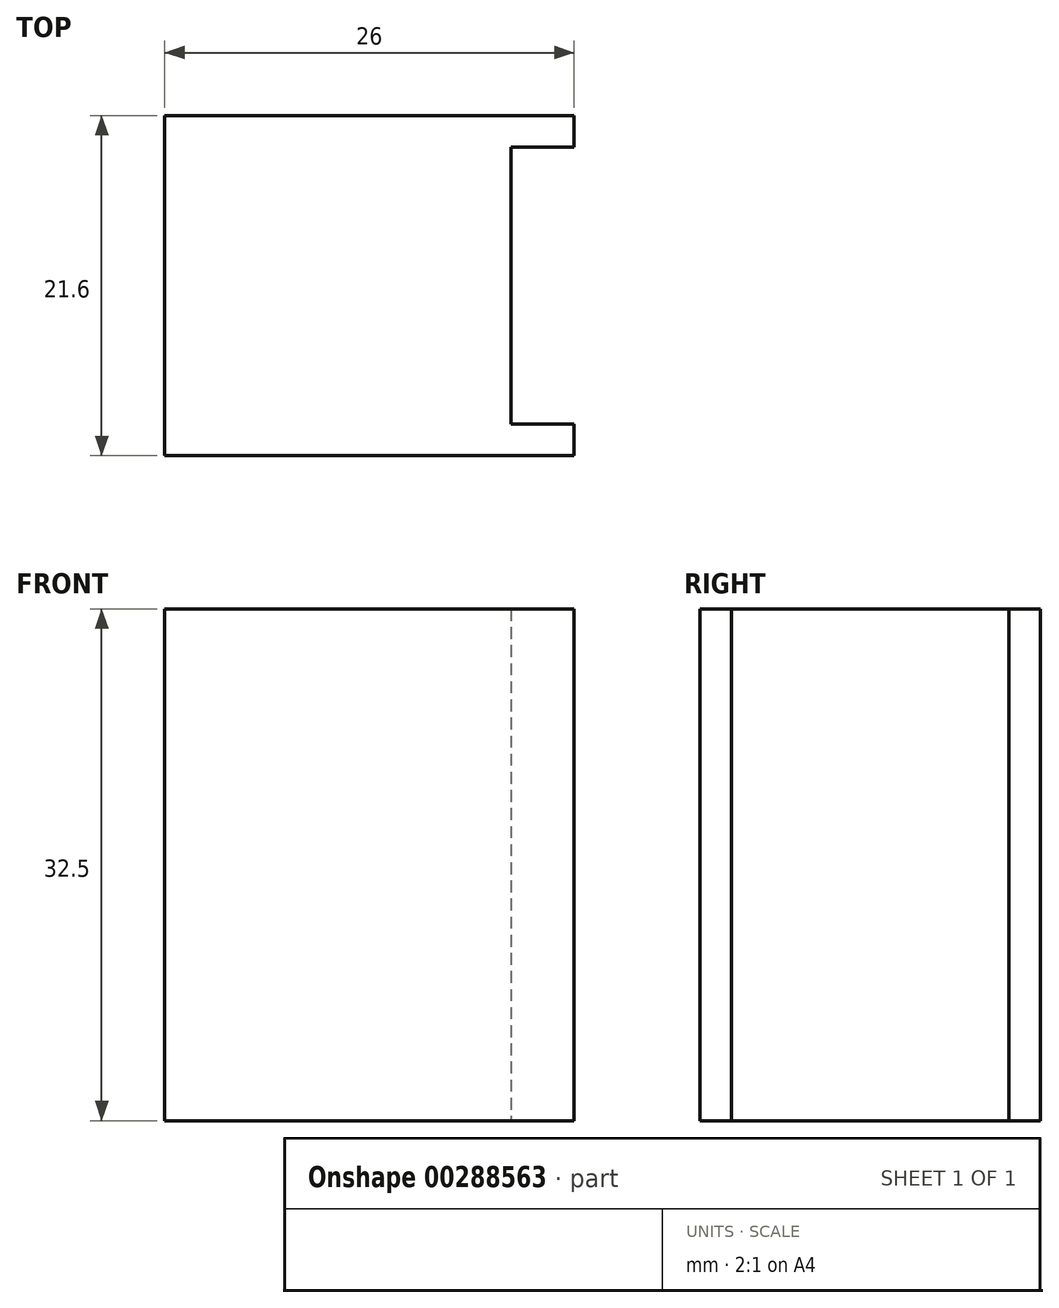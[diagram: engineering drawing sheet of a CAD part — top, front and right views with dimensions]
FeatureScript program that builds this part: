
annotation { "Feature Type Name" : "Feature", "Feature Type Description" : "" }
export const myFeature = defineFeature(function(context is Context, id is Id, definition is map)
    precondition{}
    {
        {
            var Q0;
            Q0=qCreatedBy(makeId("Top.planeOp"),FACE);
            var sketch = newSketch(context, id + "F0", { "sketchPlane" : qUnion([Q0])});
            skLineSegment(sketch, "E0.bottom", {"start": v(11, 10.8) * mm, "end": v(-11, 10.8) * mm});
            skLineSegment(sketch, "E0.top", {"start": v(11, -10.8) * mm, "end": v(-11, -10.8) * mm});
            skLineSegment(sketch, "E0.left", {"start": v(11, 10.8) * mm, "end": v(11, -10.8) * mm});
            skLineSegment(sketch, "E0.right", {"start": v(-11, 10.8) * mm, "end": v(-11, -10.8) * mm});
            skPoint(sketch, "E0.middle", {"position": v(0, 0) * mm});
            skLineSegment(sketch, "E1.bottom", {"start": v(11, 10.8) * mm, "end": v(15, 10.8) * mm});
            skLineSegment(sketch, "E1.top", {"start": v(11, 8.8) * mm, "end": v(15, 8.8) * mm});
            skLineSegment(sketch, "E1.left", {"start": v(11, 10.8) * mm, "end": v(11, 8.8) * mm});
            skLineSegment(sketch, "E1.right", {"start": v(15, 10.8) * mm, "end": v(15, 8.8) * mm});
            skLineSegment(sketch, "E2.MirrorCS", {"start": v(11, -8.8) * mm, "end": v(15, -8.8) * mm});
            skLineSegment(sketch, "E3.MirrorCS", {"start": v(11, -10.8) * mm, "end": v(15, -10.8) * mm});
            skLineSegment(sketch, "E4.MirrorCS", {"start": v(15, -10.8) * mm, "end": v(15, -8.8) * mm});
            skSolve(sketch);
        }
        {
            var Q0;
            {var subQ4=sQuery(id+"F0.wireOp",EDGE,"E0.bottom");Q0=makeQuery(id+"F0.imprint","IMPRINT",FACE,{"disambiguationData":[TD([[makeQuery(id+"F0.imprint","IMPRINT",EDGE,{"derivedFrom":subQ4}),1.0]])]});}
            var Q1;
            {var subQ0=sQuery(id+"F0.wireOp",EDGE,"E1.bottom");Q1=makeQuery(id+"F0.imprint","IMPRINT",FACE,{"disambiguationData":[TD([[makeQuery(id+"F0.imprint","IMPRINT",EDGE,{"derivedFrom":subQ0}),-1.0]])]});}
            var Q2;
            {var subQ2=sQuery(id+"F0.wireOp",EDGE,"E2.MirrorCS");Q2=makeQuery(id+"F0.imprint","IMPRINT",FACE,{"disambiguationData":[TD([[makeQuery(id+"F0.imprint","IMPRINT",EDGE,{"derivedFrom":subQ2}),-1.0]])]});}
            extrude(context, id + "F1", {"entities" : qUnion([Q0, Q1, Q2]), "depth" : 32.5 * mm, "offsetDistance" : 25 * mm});
        }
    });
